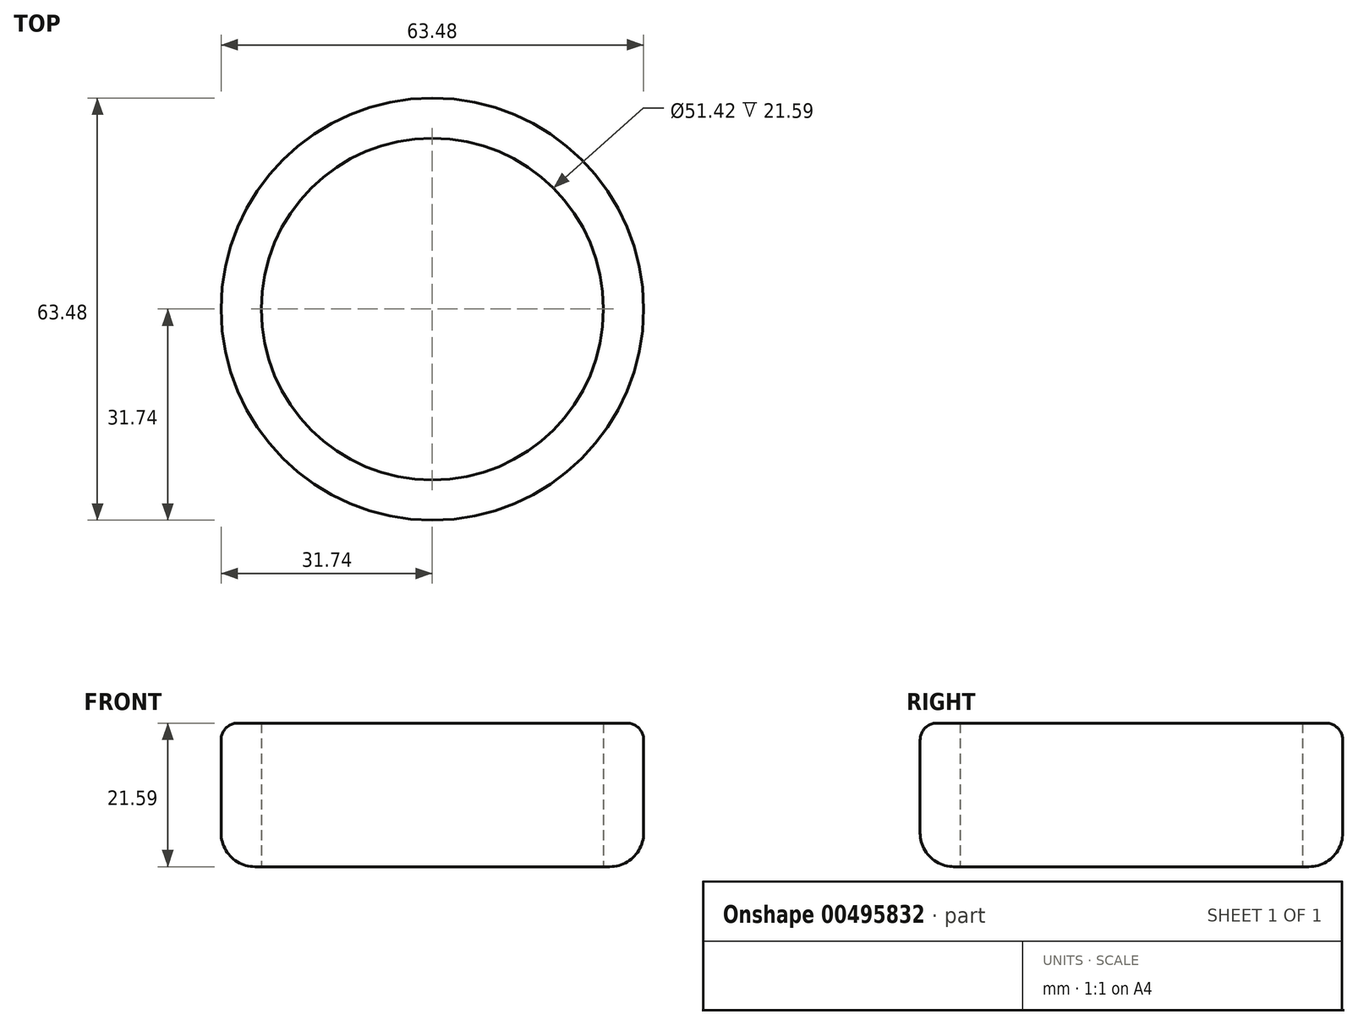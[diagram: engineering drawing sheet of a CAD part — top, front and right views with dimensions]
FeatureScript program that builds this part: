
annotation { "Feature Type Name" : "Feature", "Feature Type Description" : "" }
export const myFeature = defineFeature(function(context is Context, id is Id, definition is map)
    precondition{}
    {
        {
            var Q0;
            Q0=qCreatedBy(makeId("Top.planeOp"),FACE);
            var sketch = newSketch(context, id + "F0", { "sketchPlane" : qUnion([Q0])});
            skCircle(sketch, "E0", {"center": v(0, 0) * mm, "radius": 31.74 * mm});
            skCircle(sketch, "E1", {"center": v(0, 0) * mm, "radius": 25.71 * mm});
            skLineSegment(sketch, "E2", {"start": v(0, 0) * mm, "end": v(25.71, 0) * mm});
            skLineSegment(sketch, "E3", {"start": v(25.71, 0) * mm, "end": v(0, 0) * mm});
            skLineSegment(sketch, "E4", {"start": v(0, 0) * mm, "end": v(-25.71, 0) * mm});
            skLineSegment(sketch, "E5", {"start": v(-25.71, 0) * mm, "end": v(0, 0) * mm});
            skLineSegment(sketch, "E6", {"start": v(0, 25.71) * mm, "end": v(0, -25.71) * mm});
            skLineSegment(sketch, "E7", {"start": v(0, 0) * mm, "end": v(18.48, 17.87) * mm});
            skLineSegment(sketch, "E8", {"start": v(18.48, 17.87) * mm, "end": v(-18.2, -18.16) * mm});
            skLineSegment(sketch, "E9", {"start": v(-18.2, -18.16) * mm, "end": v(0, 0) * mm});
            skLineSegment(sketch, "E10", {"start": v(-16.38, 19.82) * mm, "end": v(15.86, -20.24) * mm});
            skLineSegment(sketch, "E11", {"start": v(15.86, -20.24) * mm, "end": v(0, 0) * mm});
            skSolve(sketch);
        }
        {
            var Q0;
            Q0 = qSketchRegion(id + "F0", true);
            extrude(context, id + "F1", {"entities" : qUnion([Q0]), "depth" : 21.59 * mm});
        }
        {
            var Q0;
            Q0=makeQuery(id+"F1.opExtrude","CAP_EDGE",EDGE,{"disambiguationData":[OSD([sQuery(id+"F0.wireOp",EDGE,"E0")])],"isStart":true});
            fillet(context, id + "F2", {"entities" : qUnion([Q0]), "radius" : 5.08 * mm, "tangentPropagation" : true, "allowEdgeOverflow" : false});
        }
        {
            var Q0;
            Q0=makeQuery(id+"F1.opExtrude","CAP_EDGE",EDGE,{"disambiguationData":[OSD([sQuery(id+"F0.wireOp",EDGE,"E0")])],"isStart":false});
            fillet(context, id + "F3", {"entities" : qUnion([Q0]), "radius" : 2.54 * mm, "tangentPropagation" : true, "allowEdgeOverflow" : false});
        }
    });
